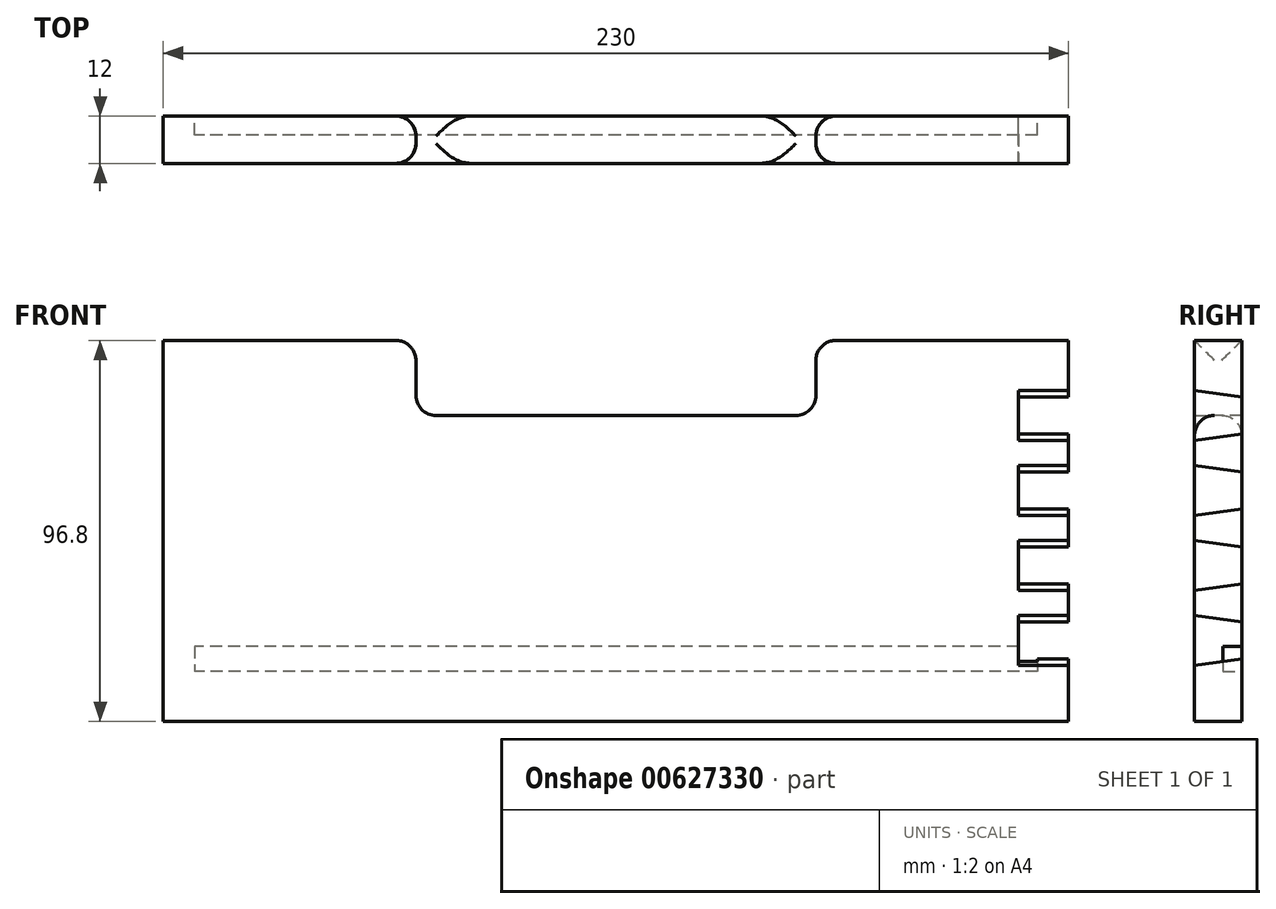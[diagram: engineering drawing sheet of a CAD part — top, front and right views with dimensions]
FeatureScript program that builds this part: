
annotation { "Feature Type Name" : "Feature", "Feature Type Description" : "" }
export const myFeature = defineFeature(function(context is Context, id is Id, definition is map)
    precondition{}
    {
        {
            var Q0;
            Q0=qCreatedBy(makeId("Front.planeOp"),FACE);
            var sketch = newSketch(context, id + "F0", { "sketchPlane" : qUnion([Q0])});
            skLineSegment(sketch, "E0.bottom", {"start": v(-115, 48.4) * mm, "end": v(115, 48.4) * mm});
            skLineSegment(sketch, "E0.top", {"start": v(-115, -48.4) * mm, "end": v(115, -48.4) * mm});
            skLineSegment(sketch, "E0.left", {"start": v(-115, 48.4) * mm, "end": v(-115, -48.4) * mm});
            skLineSegment(sketch, "E0.right", {"start": v(115, 48.4) * mm, "end": v(115, -48.4) * mm});
            skPoint(sketch, "E0.middle", {"position": v(0, 0) * mm});
            skSolve(sketch);
        }
        {
            var Q0;
            Q0 = qSketchRegion(id + "F0", true);
            extrude(context, id + "F1", {"entities" : qUnion([Q0]), "oppositeDirection" : true, "depth" : 12 * mm, "offsetDistance" : 25.4 * mm});
        }
        {
            var Q0;
            Q0=makeQuery(id+"F1.opExtrude","CAP_FACE",FACE,{"disambiguationData":[OSD([sQuery(id+"F0.wireOp",EDGE,"E0.bottom"),sQuery(id+"F0.wireOp",EDGE,"E0.top"),sQuery(id+"F0.wireOp",EDGE,"E0.left"),sQuery(id+"F0.wireOp",EDGE,"E0.right")])],"isStart":true});
            var sketch = newSketch(context, id + "F2", { "sketchPlane" : qUnion([Q0])});
            skLineSegment(sketch, "E1.bottom", {"start": v(-50.8, 48.4) * mm, "end": v(50.8, 48.4) * mm});
            skLineSegment(sketch, "E1.top", {"start": v(-50.8, 29.35) * mm, "end": v(50.8, 29.35) * mm});
            skLineSegment(sketch, "E1.left", {"start": v(-50.8, 48.4) * mm, "end": v(-50.8, 29.35) * mm});
            skLineSegment(sketch, "E1.right", {"start": v(50.8, 48.4) * mm, "end": v(50.8, 29.35) * mm});
            skPoint(sketch, "E1.middle", {"position": v(0, 38.88) * mm});
            skSolve(sketch);
        }
        {
            var Q0;
            Q0 = qSketchRegion(id + "F2", true);
            extrude(context, id + "F3", {"entities" : qUnion([Q0]), "operationType" : NewBodyOperationType.REMOVE, "endBound" : BoundingType.UP_TO_NEXT, "oppositeDirection" : true, "depth" : 25.4 * mm, "offsetDistance" : 25.4 * mm});
        }
        {
            var Q0;
            Q0=makeQuery(id+"F3.boolean.opBoolean","COPY",FACE,{"derivedFrom":makeQuery(id+"F3.opExtrude","SWEPT_FACE",FACE,{"disambiguationData":[OSD([sQuery(id+"F2.wireOp",EDGE,"E1.left")])]})});
            var Q1;
            Q1=makeQuery(id+"F3.boolean.opBoolean","COPY",FACE,{"derivedFrom":makeQuery(id+"F3.opExtrude","SWEPT_FACE",FACE,{"disambiguationData":[OSD([sQuery(id+"F2.wireOp",EDGE,"E1.right")])]})});
            fillet(context, id + "F4", {"entities" : qUnion([Q0, Q1]), "radius" : 5.08 * mm, "tangentPropagation" : true, "allowEdgeOverflow" : false});
        }
        {
            var Q0;
            Q0=makeQuery(id+"F1.opExtrude","SWEPT_FACE",FACE,{"disambiguationData":[OSD([sQuery(id+"F0.wireOp",EDGE,"E0.right")])]});
            var sketch = newSketch(context, id + "F5", { "sketchPlane" : qUnion([Q0])});
            skLineSegment(sketch, "E2", {"start": v(0, 35.7) * mm, "end": v(12, 34.02) * mm});
            skLineSegment(sketch, "E3", {"start": v(12, 34.02) * mm, "end": v(12, 24.69) * mm});
            skLineSegment(sketch, "E4", {"start": v(12, 24.69) * mm, "end": v(0, 23) * mm});
            skLineSegment(sketch, "E5", {"start": v(0, 23) * mm, "end": v(0, 35.7) * mm});
            skLineSegment(sketch, "E6.0.1.0", {"start": v(12, 5.64) * mm, "end": v(0, 3.95) * mm});
            skLineSegment(sketch, "E6.0.1.1", {"start": v(12, 14.97) * mm, "end": v(12, 5.64) * mm});
            skLineSegment(sketch, "E6.0.1.2", {"start": v(0, 16.65) * mm, "end": v(12, 14.97) * mm});
            skLineSegment(sketch, "E6.0.1.3", {"start": v(0, 3.95) * mm, "end": v(0, 16.65) * mm});
            skLineSegment(sketch, "E6.0.2.0", {"start": v(12, -13.41) * mm, "end": v(0, -15.1) * mm});
            skLineSegment(sketch, "E6.0.2.1", {"start": v(12, -4.08) * mm, "end": v(12, -13.41) * mm});
            skLineSegment(sketch, "E6.0.2.2", {"start": v(0, -2.4) * mm, "end": v(12, -4.08) * mm});
            skLineSegment(sketch, "E6.0.2.3", {"start": v(0, -15.1) * mm, "end": v(0, -2.4) * mm});
            skLineSegment(sketch, "E6.0.3.0", {"start": v(12, -32.46) * mm, "end": v(0, -34.15) * mm});
            skLineSegment(sketch, "E6.0.3.1", {"start": v(12, -23.13) * mm, "end": v(12, -32.46) * mm});
            skLineSegment(sketch, "E6.0.3.2", {"start": v(0, -21.45) * mm, "end": v(12, -23.13) * mm});
            skLineSegment(sketch, "E6.0.3.3", {"start": v(0, -34.15) * mm, "end": v(0, -21.45) * mm});
            skLineSegment(sketch, "E6.direction1", {"start": v(0, 23) * mm, "end": v(25.4, 23) * mm, "construction": true});
            skLineSegment(sketch, "E6.direction2", {"start": v(0, 23) * mm, "end": v(0, 3.95) * mm, "construction": true});
            skSolve(sketch);
        }
        {
            var Q0;
            Q0=makeQuery(id+"F5.imprint","IMPRINT",FACE,{"disambiguationData":[TD([[makeQuery(id+"F5.imprint","IMPRINT",EDGE,{"derivedFrom":sQuery(id+"F5.wireOp",EDGE,"E2")}),-1.0]])]});
            var Q1;
            Q1=makeQuery(id+"F5.imprint","IMPRINT",FACE,{"disambiguationData":[TD([[makeQuery(id+"F5.imprint","IMPRINT",EDGE,{"derivedFrom":sQuery(id+"F5.wireOp",EDGE,"E6.0.1.0")}),-1.0]])]});
            var Q2;
            Q2=makeQuery(id+"F5.imprint","IMPRINT",FACE,{"disambiguationData":[TD([[makeQuery(id+"F5.imprint","IMPRINT",EDGE,{"derivedFrom":sQuery(id+"F5.wireOp",EDGE,"E6.0.2.0")}),-1.0]])]});
            var Q3;
            Q3=makeQuery(id+"F5.imprint","IMPRINT",FACE,{"disambiguationData":[TD([[makeQuery(id+"F5.imprint","IMPRINT",EDGE,{"derivedFrom":sQuery(id+"F5.wireOp",EDGE,"E6.0.3.0")}),-1.0]])]});
            extrude(context, id + "F6", {"entities" : qUnion([Q0, Q1, Q2, Q3]), "operationType" : NewBodyOperationType.REMOVE, "oppositeDirection" : true, "depth" : 12.7 * mm, "offsetDistance" : 25.4 * mm});
        }
        {
            var Q0;
            Q0=makeQuery(id+"F1.opExtrude","CAP_FACE",FACE,{"disambiguationData":[OSD([sQuery(id+"F0.wireOp",EDGE,"E0.bottom"),sQuery(id+"F0.wireOp",EDGE,"E0.top"),sQuery(id+"F0.wireOp",EDGE,"E0.left"),sQuery(id+"F0.wireOp",EDGE,"E0.right")])],"isStart":false});
            var sketch = newSketch(context, id + "F7", { "sketchPlane" : qUnion([Q0])});
            skLineSegment(sketch, "E7.bottom", {"start": v(-102.3, -35.7) * mm, "end": v(102.3, -35.7) * mm});
            skLineSegment(sketch, "E7.top", {"start": v(-102.3, -29.35) * mm, "end": v(102.3, -29.35) * mm});
            skLineSegment(sketch, "E7.left", {"start": v(-102.3, -35.7) * mm, "end": v(-102.3, -29.35) * mm});
            skLineSegment(sketch, "E7.right", {"start": v(102.3, -35.7) * mm, "end": v(102.3, -29.35) * mm});
            skPoint(sketch, "E7.middle", {"position": v(0, -32.53) * mm});
            skLineSegment(sketch, "E8.bottom", {"start": v(-102.3, -29.35) * mm, "end": v(-107.06, -29.35) * mm});
            skLineSegment(sketch, "E8.top", {"start": v(-102.3, -35.7) * mm, "end": v(-107.06, -35.7) * mm});
            skLineSegment(sketch, "E8.left", {"start": v(-102.3, -29.35) * mm, "end": v(-102.3, -35.7) * mm});
            skLineSegment(sketch, "E8.right", {"start": v(-107.06, -29.35) * mm, "end": v(-107.06, -35.7) * mm});
            skLineSegment(sketch, "E9.MirrorCS", {"start": v(102.3, -29.35) * mm, "end": v(102.3, -35.7) * mm});
            skLineSegment(sketch, "E10.MirrorCS", {"start": v(102.3, -29.35) * mm, "end": v(107.06, -29.35) * mm});
            skLineSegment(sketch, "E11.MirrorCS", {"start": v(107.06, -29.35) * mm, "end": v(107.06, -35.7) * mm});
            skLineSegment(sketch, "E12.MirrorCS", {"start": v(102.3, -35.7) * mm, "end": v(107.06, -35.7) * mm});
            skSolve(sketch);
        }
        {
            var Q0;
            Q0 = qSketchRegion(id + "F7", true);
            extrude(context, id + "F8", {"entities" : qUnion([Q0]), "operationType" : NewBodyOperationType.REMOVE, "oppositeDirection" : true, "depth" : 4.76 * mm, "offsetDistance" : 25.4 * mm});
        }
    });
